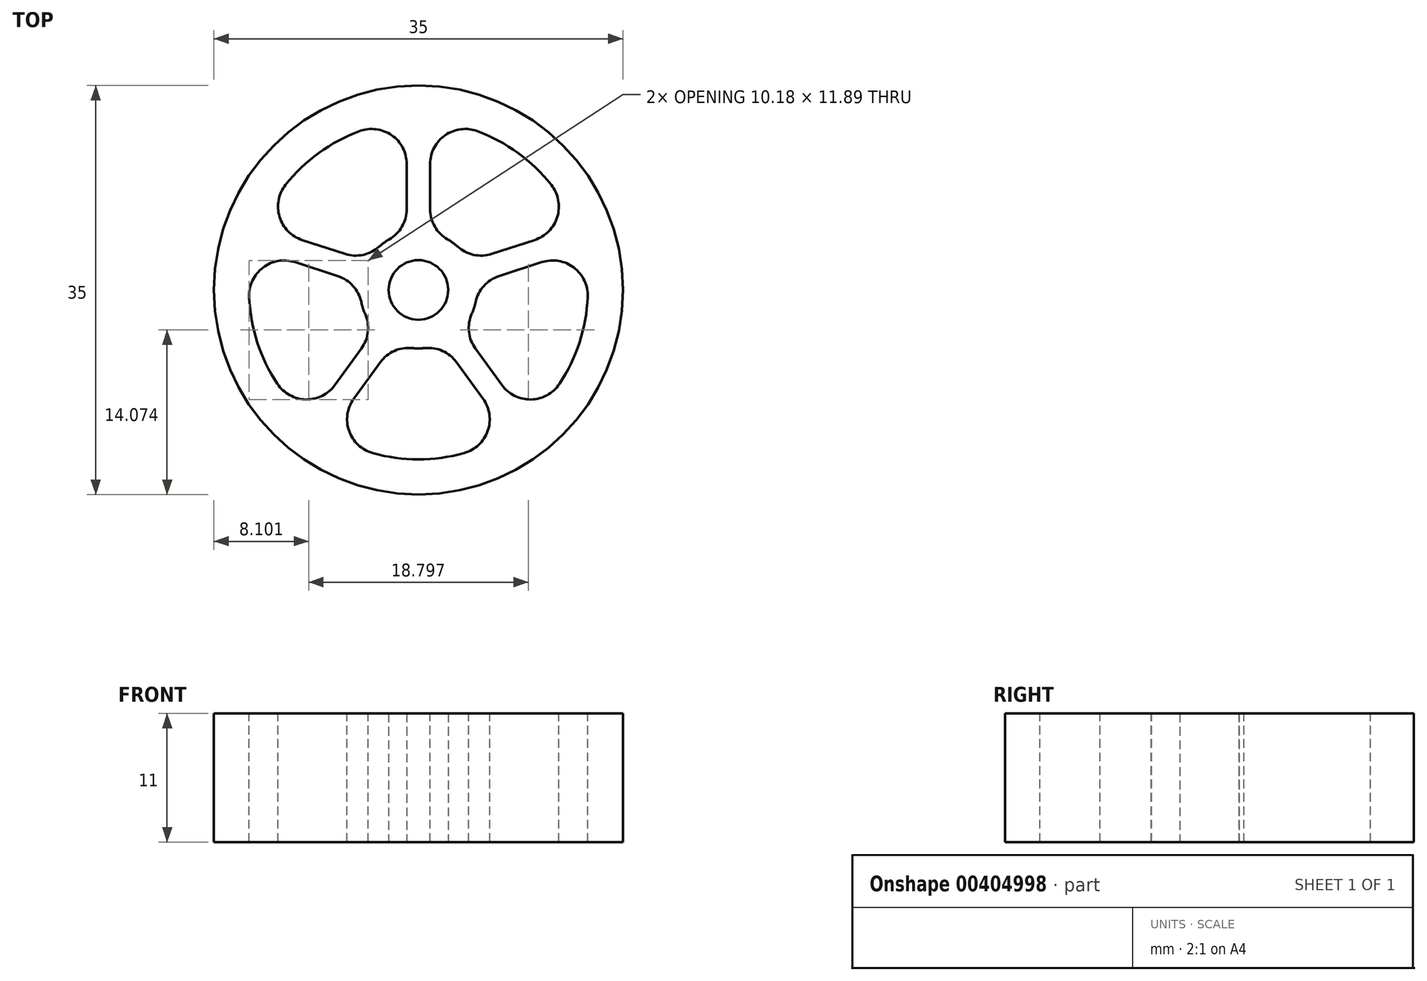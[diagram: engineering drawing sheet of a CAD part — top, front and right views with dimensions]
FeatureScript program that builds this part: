
annotation { "Feature Type Name" : "Feature", "Feature Type Description" : "" }
export const myFeature = defineFeature(function(context is Context, id is Id, definition is map)
    precondition{}
    {
        {
            var Q0;
            Q0=qCreatedBy(makeId("Top.planeOp"),FACE);
            var sketch = newSketch(context, id + "F0", { "sketchPlane" : qUnion([Q0])});
            skCircle(sketch, "E0", {"center": v(0, 0) * mm, "radius": 17.5 * mm});
            skCircle(sketch, "E1", {"center": v(0, 0) * mm, "radius": 2.55 * mm});
            skSolve(sketch);
        }
        {
            var Q0;
            Q0=makeQuery(id+"F0.imprint","IMPRINT",FACE,{"disambiguationData":[TD([[makeQuery(id+"F0.imprint","IMPRINT",EDGE,{"derivedFrom":sQuery(id+"F0.wireOp",EDGE,"E0")}),1.0]])]});
            extrude(context, id + "F1", {"entities" : qUnion([Q0]), "depth" : 11 * mm});
        }
        {
            var Q0;
            Q0=makeQuery(id+"F1.opExtrude","CAP_FACE",FACE,{"disambiguationData":[OSD([sQuery(id+"F0.wireOp",EDGE,"E0"),sQuery(id+"F0.wireOp",EDGE,"E1")])],"isStart":false});
            var sketch = newSketch(context, id + "F2", { "sketchPlane" : qUnion([Q0])});
            skCircle(sketch, "E2", {"center": v(0, 0) * mm, "radius": 14.5 * mm});
            skCircle(sketch, "E3", {"center": v(0, 0) * mm, "radius": 5 * mm});
            skLineSegment(sketch, "E4", {"start": v(0, 5) * mm, "end": v(0, 14.5) * mm, "construction": true});
            skLineSegment(sketch, "E5.0", {"start": v(1, 4.9) * mm, "end": v(1, 14.47) * mm});
            skLineSegment(sketch, "E6.0", {"start": v(-1, 4.9) * mm, "end": v(-1, 14.47) * mm});
            skLineSegment(sketch, "E7.1.0", {"start": v(-4.97, 0.56) * mm, "end": v(-14.07, 3.52) * mm});
            skLineSegment(sketch, "E7.1.1", {"start": v(-4.35, 2.46) * mm, "end": v(-13.45, 5.42) * mm});
            skLineSegment(sketch, "E7.2.0", {"start": v(-2.07, -4.55) * mm, "end": v(-7.7, -12.3) * mm});
            skLineSegment(sketch, "E7.2.1", {"start": v(-3.69, -3.38) * mm, "end": v(-9.31, -11.12) * mm});
            skLineSegment(sketch, "E7.3.0", {"start": v(3.69, -3.38) * mm, "end": v(9.31, -11.12) * mm});
            skLineSegment(sketch, "E7.3.1", {"start": v(2.07, -4.55) * mm, "end": v(7.7, -12.3) * mm});
            skLineSegment(sketch, "E7.4.0", {"start": v(4.35, 2.46) * mm, "end": v(13.45, 5.42) * mm});
            skLineSegment(sketch, "E7.4.1", {"start": v(4.97, 0.56) * mm, "end": v(14.07, 3.52) * mm});
            skSolve(sketch);
        }
        {
            var Q0;
            {var subQ0=sQuery(id+"F2.wireOp",EDGE,"E6.0");Q0=makeQuery(id+"F2.imprint","IMPRINT",FACE,{"disambiguationData":[TD([[makeQuery(id+"F2.imprint","IMPRINT",EDGE,{"derivedFrom":subQ0}),1.0]])]});}
            var Q1;
            {var subQ0=sQuery(id+"F2.wireOp",EDGE,"E5.0");Q1=makeQuery(id+"F2.imprint","IMPRINT",FACE,{"disambiguationData":[TD([[makeQuery(id+"F2.imprint","IMPRINT",EDGE,{"derivedFrom":subQ0}),-1.0]])]});}
            var Q2;
            {var subQ0=sQuery(id+"F2.wireOp",EDGE,"E7.3.0");Q2=makeQuery(id+"F2.imprint","IMPRINT",FACE,{"disambiguationData":[TD([[makeQuery(id+"F2.imprint","IMPRINT",EDGE,{"derivedFrom":subQ0}),1.0]])]});}
            var Q3;
            {var subQ0=sQuery(id+"F2.wireOp",EDGE,"E7.2.0");Q3=makeQuery(id+"F2.imprint","IMPRINT",FACE,{"disambiguationData":[TD([[makeQuery(id+"F2.imprint","IMPRINT",EDGE,{"derivedFrom":subQ0}),1.0]])]});}
            var Q4;
            {var subQ0=sQuery(id+"F2.wireOp",EDGE,"E7.1.0");Q4=makeQuery(id+"F2.imprint","IMPRINT",FACE,{"disambiguationData":[TD([[makeQuery(id+"F2.imprint","IMPRINT",EDGE,{"derivedFrom":subQ0}),1.0]])]});}
            extrude(context, id + "F3", {"entities" : qUnion([Q0, Q1, Q2, Q3, Q4]), "operationType" : NewBodyOperationType.REMOVE, "oppositeDirection" : true, "depth" : 25 * mm});
        }
        {
            var Q0;
            Q0=makeQuery(id+"F3.boolean.opBoolean","COPY",EDGE,{"derivedFrom":makeQuery(id+"F3.opExtrude","SWEPT_EDGE",EDGE,{"disambiguationData":[OSD([sQuery(id+"F2.wireOp",EDGE,"E3"),sQuery(id+"F2.wireOp",EDGE,"E6.0")])]})});
            var Q1;
            Q1=makeQuery(id+"F3.boolean.opBoolean","COPY",EDGE,{"derivedFrom":makeQuery(id+"F3.opExtrude","SWEPT_EDGE",EDGE,{"disambiguationData":[OSD([sQuery(id+"F2.wireOp",EDGE,"E3"),sQuery(id+"F2.wireOp",EDGE,"E7.1.1")])]})});
            var Q2;
            Q2=makeQuery(id+"F3.boolean.opBoolean","COPY",EDGE,{"derivedFrom":makeQuery(id+"F3.opExtrude","SWEPT_EDGE",EDGE,{"disambiguationData":[OSD([sQuery(id+"F2.wireOp",EDGE,"E3"),sQuery(id+"F2.wireOp",EDGE,"E5.0")])]})});
            var Q3;
            Q3=makeQuery(id+"F3.boolean.opBoolean","COPY",EDGE,{"derivedFrom":makeQuery(id+"F3.opExtrude","SWEPT_EDGE",EDGE,{"disambiguationData":[OSD([sQuery(id+"F2.wireOp",EDGE,"E3"),sQuery(id+"F2.wireOp",EDGE,"E7.4.0")])]})});
            var Q4;
            Q4=makeQuery(id+"F3.boolean.opBoolean","COPY",EDGE,{"derivedFrom":makeQuery(id+"F3.opExtrude","SWEPT_EDGE",EDGE,{"disambiguationData":[OSD([sQuery(id+"F2.wireOp",EDGE,"E3"),sQuery(id+"F2.wireOp",EDGE,"E7.3.0")])]})});
            var Q5;
            Q5=makeQuery(id+"F3.boolean.opBoolean","COPY",EDGE,{"derivedFrom":makeQuery(id+"F3.opExtrude","SWEPT_EDGE",EDGE,{"disambiguationData":[OSD([sQuery(id+"F2.wireOp",EDGE,"E3"),sQuery(id+"F2.wireOp",EDGE,"E7.4.1")])]})});
            var Q6;
            Q6=makeQuery(id+"F3.boolean.opBoolean","COPY",EDGE,{"derivedFrom":makeQuery(id+"F3.opExtrude","SWEPT_EDGE",EDGE,{"disambiguationData":[OSD([sQuery(id+"F2.wireOp",EDGE,"E3"),sQuery(id+"F2.wireOp",EDGE,"E7.3.1")])]})});
            var Q7;
            Q7=makeQuery(id+"F3.boolean.opBoolean","COPY",EDGE,{"derivedFrom":makeQuery(id+"F3.opExtrude","SWEPT_EDGE",EDGE,{"disambiguationData":[OSD([sQuery(id+"F2.wireOp",EDGE,"E3"),sQuery(id+"F2.wireOp",EDGE,"E7.2.0")])]})});
            var Q8;
            Q8=makeQuery(id+"F3.boolean.opBoolean","COPY",EDGE,{"derivedFrom":makeQuery(id+"F3.opExtrude","SWEPT_EDGE",EDGE,{"disambiguationData":[OSD([sQuery(id+"F2.wireOp",EDGE,"E3"),sQuery(id+"F2.wireOp",EDGE,"E7.1.0")])]})});
            var Q9;
            Q9=makeQuery(id+"F3.boolean.opBoolean","COPY",EDGE,{"derivedFrom":makeQuery(id+"F3.opExtrude","SWEPT_EDGE",EDGE,{"disambiguationData":[OSD([sQuery(id+"F2.wireOp",EDGE,"E3"),sQuery(id+"F2.wireOp",EDGE,"E7.2.1")])]})});
            var Q10;
            Q10=makeQuery(id+"F3.boolean.opBoolean","COPY",EDGE,{"derivedFrom":makeQuery(id+"F3.opExtrude","SWEPT_EDGE",EDGE,{"disambiguationData":[OSD([sQuery(id+"F2.wireOp",EDGE,"E2"),sQuery(id+"F2.wireOp",EDGE,"E7.4.0")])]})});
            var Q11;
            Q11=makeQuery(id+"F3.boolean.opBoolean","COPY",EDGE,{"derivedFrom":makeQuery(id+"F3.opExtrude","SWEPT_EDGE",EDGE,{"disambiguationData":[OSD([sQuery(id+"F2.wireOp",EDGE,"E2"),sQuery(id+"F2.wireOp",EDGE,"E7.4.1")])]})});
            var Q12;
            Q12=makeQuery(id+"F3.boolean.opBoolean","COPY",EDGE,{"derivedFrom":makeQuery(id+"F3.opExtrude","SWEPT_EDGE",EDGE,{"disambiguationData":[OSD([sQuery(id+"F2.wireOp",EDGE,"E2"),sQuery(id+"F2.wireOp",EDGE,"E5.0")])]})});
            var Q13;
            Q13=makeQuery(id+"F3.boolean.opBoolean","COPY",EDGE,{"derivedFrom":makeQuery(id+"F3.opExtrude","SWEPT_EDGE",EDGE,{"disambiguationData":[OSD([sQuery(id+"F2.wireOp",EDGE,"E2"),sQuery(id+"F2.wireOp",EDGE,"E6.0")])]})});
            var Q14;
            Q14=makeQuery(id+"F3.boolean.opBoolean","COPY",EDGE,{"derivedFrom":makeQuery(id+"F3.opExtrude","SWEPT_EDGE",EDGE,{"disambiguationData":[OSD([sQuery(id+"F2.wireOp",EDGE,"E2"),sQuery(id+"F2.wireOp",EDGE,"E7.1.1")])]})});
            var Q15;
            Q15=makeQuery(id+"F3.boolean.opBoolean","COPY",EDGE,{"derivedFrom":makeQuery(id+"F3.opExtrude","SWEPT_EDGE",EDGE,{"disambiguationData":[OSD([sQuery(id+"F2.wireOp",EDGE,"E2"),sQuery(id+"F2.wireOp",EDGE,"E7.3.0")])]})});
            var Q16;
            Q16=makeQuery(id+"F3.boolean.opBoolean","COPY",EDGE,{"derivedFrom":makeQuery(id+"F3.opExtrude","SWEPT_EDGE",EDGE,{"disambiguationData":[OSD([sQuery(id+"F2.wireOp",EDGE,"E2"),sQuery(id+"F2.wireOp",EDGE,"E7.2.1")])]})});
            var Q17;
            Q17=makeQuery(id+"F3.boolean.opBoolean","COPY",EDGE,{"derivedFrom":makeQuery(id+"F3.opExtrude","SWEPT_EDGE",EDGE,{"disambiguationData":[OSD([sQuery(id+"F2.wireOp",EDGE,"E2"),sQuery(id+"F2.wireOp",EDGE,"E7.1.0")])]})});
            var Q18;
            Q18=makeQuery(id+"F3.boolean.opBoolean","COPY",EDGE,{"derivedFrom":makeQuery(id+"F3.opExtrude","SWEPT_EDGE",EDGE,{"disambiguationData":[OSD([sQuery(id+"F2.wireOp",EDGE,"E2"),sQuery(id+"F2.wireOp",EDGE,"E7.3.1")])]})});
            var Q19;
            Q19=makeQuery(id+"F3.boolean.opBoolean","COPY",EDGE,{"derivedFrom":makeQuery(id+"F3.opExtrude","SWEPT_EDGE",EDGE,{"disambiguationData":[OSD([sQuery(id+"F2.wireOp",EDGE,"E2"),sQuery(id+"F2.wireOp",EDGE,"E7.2.0")])]})});
            fillet(context, id + "F4", {"entities" : qUnion([Q0, Q1, Q2, Q3, Q4, Q5, Q6, Q7, Q8, Q9, Q10, Q11, Q12, Q13, Q14, Q15, Q16, Q17, Q18, Q19]), "radius" : 3 * mm, "tangentPropagation" : true, "allowEdgeOverflow" : false});
        }
    });
